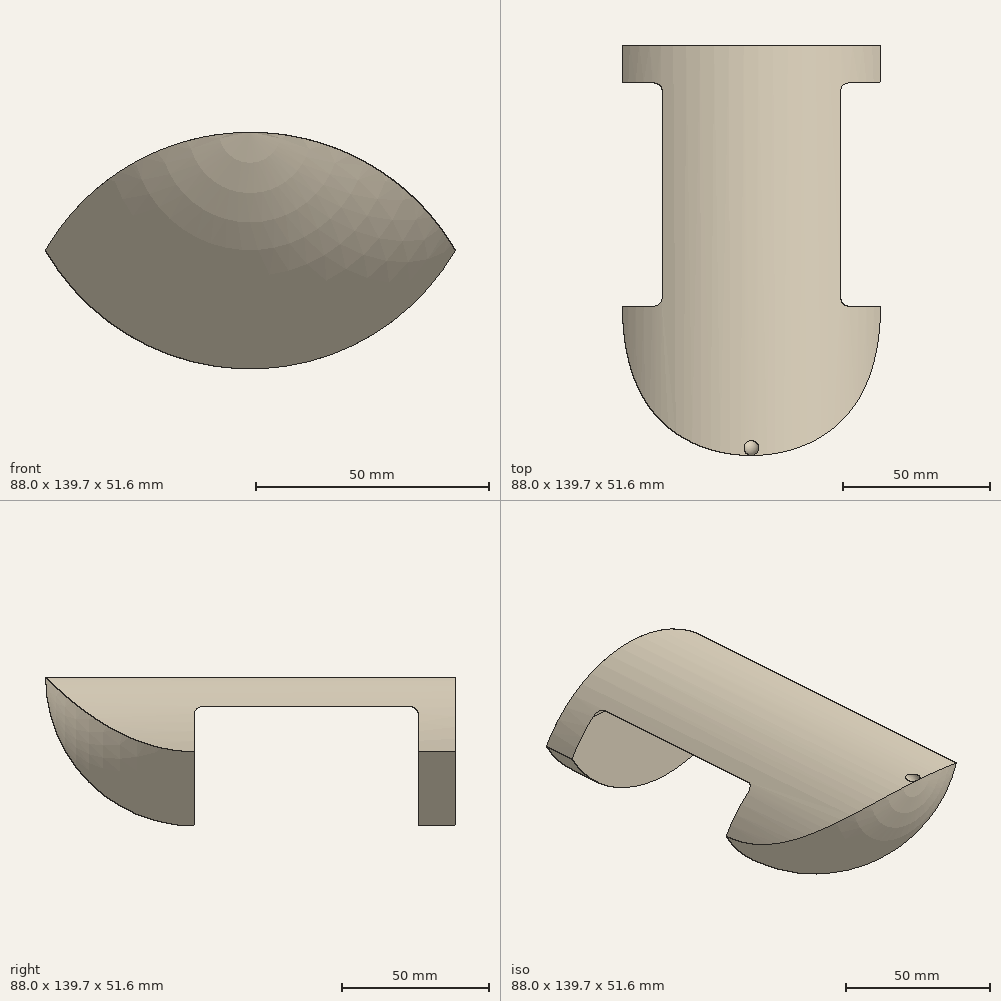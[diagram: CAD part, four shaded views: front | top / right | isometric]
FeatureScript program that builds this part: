
annotation { "Feature Type Name" : "Feature", "Feature Type Description" : "" }
export const myFeature = defineFeature(function(context is Context, id is Id, definition is map)
    precondition{}
    {
        {
            var Q0;
            Q0=qCreatedBy(makeId("Right.planeOp"),FACE);
            var sketch = newSketch(context, id + "F0", { "sketchPlane" : qUnion([Q0])});
            skLineSegment(sketch, "E0", {"start": v(0, 0) * mm, "end": v(-50.8, 0) * mm});
            skLineSegment(sketch, "E1", {"start": v(0, 0) * mm, "end": v(0, -50.8) * mm});
            skArc(sketch, "E2", {"start": v(-50.8, 0) * mm, "mid": v(-35.92, -35.92) * mm, "end": v(0, -50.8) * mm});
            skSolve(sketch);
        }
        {
            var Q0;
            Q0=makeQuery(id+"F0.imprint","IMPRINT",FACE,{"disambiguationData":[TD([[makeQuery(id+"F0.imprint","IMPRINT",EDGE,{"derivedFrom":sQuery(id+"F0.wireOp",EDGE,"E0")}),1.0]])]});
            var Q1;
            Q1=sQuery(id+"F0.wireOp",EDGE,"E0");
            revolve(context, id + "F1", {"entities" : qUnion([Q0]), "axis" : qUnion([Q1]), "revolveType" : RevolveType.SYMMETRIC, "angle" : 180 * degree});
        }
        {
            var Q0;
            Q0=qCreatedBy(makeId("Front.planeOp"),FACE);
            var sketch = newSketch(context, id + "F2", { "sketchPlane" : qUnion([Q0])});
            skPoint(sketch, "E3.0", {"position": v(50.8, 0) * mm});
            skPoint(sketch, "E4.0", {"position": v(-50.8, 0) * mm});
            skArc(sketch, "E5.0", {"start": v(50.8, 0) * mm, "mid": v(0, -50.8) * mm, "end": v(-50.8, 0) * mm});
            skLineSegment(sketch, "E6", {"start": v(50.8, 0) * mm, "end": v(50.8, -50.8) * mm, "construction": true});
            skLineSegment(sketch, "E7", {"start": v(50.8, -50.8) * mm, "end": v(-50.8, -50.8) * mm, "construction": true});
            skLineSegment(sketch, "E8", {"start": v(-50.8, -50.8) * mm, "end": v(-50.8, 0) * mm, "construction": true});
            skArc(sketch, "E9", {"start": v(50.8, -50.8) * mm, "mid": v(0, 0) * mm, "end": v(-50.8, -50.8) * mm});
            skLineSegment(sketch, "E10", {"start": v(50.8, -50.8) * mm, "end": v(50.8, 0) * mm});
            skLineSegment(sketch, "E11", {"start": v(-50.8, 0) * mm, "end": v(-50.8, -50.8) * mm});
            skSolve(sketch);
        }
        {
            var Q0;
            Q0 = qSketchRegion(id + "F2", true);
            extrude(context, id + "F3", {"entities" : qUnion([Q0]), "operationType" : NewBodyOperationType.INTERSECT, "endBound" : BoundingType.THROUGH_ALL, "depth" : 89.11 * mm});
        }
        {
            var Q0;
            Q0=makeQuery(id+"F1.opRevolve","SWEPT_FACE",FACE,{"disambiguationData":[OSD([sQuery(id+"F0.wireOp",EDGE,"E1")])]});
            extrude(context, id + "F4", {"entities" : qUnion([Q0]), "operationType" : NewBodyOperationType.ADD, "depth" : 88.9 * mm});
        }
        {
            var Q0;
            Q0=qCreatedBy(makeId("Front.planeOp"),FACE);
            var sketch = newSketch(context, id + "F5", { "sketchPlane" : qUnion([Q0])});
            skLineSegment(sketch, "E12.bottom", {"start": v(-63.5, -10.16) * mm, "end": v(63.5, -10.16) * mm});
            skLineSegment(sketch, "E12.top", {"start": v(-63.5, -73.66) * mm, "end": v(63.5, -73.66) * mm});
            skLineSegment(sketch, "E12.left", {"start": v(-63.5, -10.16) * mm, "end": v(-63.5, -73.66) * mm});
            skLineSegment(sketch, "E12.right", {"start": v(63.5, -10.16) * mm, "end": v(63.5, -73.66) * mm});
            skSolve(sketch);
        }
        {
            var Q0;
            Q0 = qSketchRegion(id + "F5", true);
            extrude(context, id + "F6", {"entities" : qUnion([Q0]), "operationType" : NewBodyOperationType.REMOVE, "oppositeDirection" : true, "depth" : 76.2 * mm});
        }
        {
            var Q0;
            Q0=qCreatedBy(makeId("Top.planeOp"),FACE);
            var sketch = newSketch(context, id + "F7", { "sketchPlane" : qUnion([Q0])});
            skFitSpline(sketch, "E13.0", {"points": [v(44, 0) * mm, v(44, -1.7) * mm, v(43.95, -3.4) * mm, v(43.85, -5.07) * mm, v(43.75, -6.75) * mm, v(43.6, -8.4) * mm, v(43.4, -10.04) * mm, v(43, -13.43) * mm, v(42.4, -16.62) * mm, v(41.58, -19.61) * mm, v(40.73, -22.74) * mm, v(39.67, -25.63) * mm, v(38.39, -28.28) * mm, v(37.05, -31.05) * mm, v(35.47, -33.57) * mm, v(33.66, -35.85) * mm, v(31.79, -38.2) * mm, v(29.67, -40.28) * mm, v(27.3, -42.1) * mm, v(26.1, -43.02) * mm, v(24.84, -43.87) * mm, v(23.52, -44.65) * mm, v(22.2, -45.44) * mm, v(20.83, -46.15) * mm, v(19.4, -46.8) * mm, v(17.95, -47.44) * mm, v(16.45, -48.02) * mm, v(14.9, -48.51) * mm, v(13.35, -49.01) * mm, v(11.77, -49.43) * mm, v(10.14, -49.77) * mm, v(8.52, -50.1) * mm, v(6.88, -50.36) * mm, v(5.22, -50.53) * mm, v(3.53, -50.7) * mm, v(1.83, -50.8) * mm, v(0.13, -50.8) * mm, v(-1.56, -50.8) * mm, v(-3.25, -50.72) * mm, v(-4.92, -50.56) * mm, v(-6.6, -50.4) * mm, v(-8.26, -50.15) * mm, v(-9.9, -49.82) * mm, v(-11.53, -49.49) * mm, v(-13.13, -49.07) * mm, v(-14.7, -48.58) * mm, v(-16.24, -48.1) * mm, v(-17.74, -47.53) * mm, v(-19.2, -46.88) * mm, v(-20.65, -46.24) * mm, v(-22.05, -45.52) * mm, v(-23.4, -44.73) * mm, v(-24.72, -43.95) * mm, v(-26, -43.1) * mm, v(-27.2, -42.17) * mm, v(-29.59, -40.35) * mm, v(-31.72, -38.26) * mm, v(-33.6, -35.92) * mm, v(-35.43, -33.64) * mm, v(-37.02, -31.11) * mm, v(-38.36, -28.34) * mm, v(-39.65, -25.68) * mm, v(-40.71, -22.8) * mm, v(-41.57, -19.66) * mm, v(-42.38, -16.67) * mm, v(-43, -13.47) * mm, v(-43.4, -10.07) * mm, v(-43.6, -8.44) * mm, v(-43.75, -6.78) * mm, v(-43.85, -5.08) * mm, v(-43.94, -3.4) * mm, v(-44, -1.7) * mm, v(-44, 0) * mm], "construction": true});
            skPoint(sketch, "E14.first.point", {"position": v(0, -50.8) * mm});
            skPoint(sketch, "E14.second.point", {"position": v(0, -50.8) * mm});
            skLineSegment(sketch, "E15", {"start": v(0, -50.8) * mm, "end": v(0, 0) * mm, "construction": true});
            skLineSegment(sketch, "E16", {"start": v(0, 0) * mm, "end": v(0.1, 0.91) * mm, "construction": true});
            skArc(sketch, "E17", {"start": v(0, -45.72) * mm, "mid": v(-2.54, -48.26) * mm, "end": v(0, -50.8) * mm});
            skLineSegment(sketch, "E18", {"start": v(0, -50.8) * mm, "end": v(0, -45.72) * mm});
            skSolve(sketch);
        }
        {
            var Q0;
            Q0 = qSketchRegion(id + "F7", true);
            var Q1;
            Q1=makeQuery(id+"F7.imprint","IMPRINT",FACE,{"disambiguationData":[TD([[makeQuery(id+"F7.imprint","IMPRINT",EDGE,{"derivedFrom":sQuery(id+"F7.wireOp",EDGE,"E17")}),1.0]])]});
            var Q2;
            Q2=sQuery(id+"F7.wireOp",EDGE,"E15");
            revolve(context, id + "F8", {"operationType" : NewBodyOperationType.ADD, "entities" : qUnion([Q0, Q1]), "axis" : qUnion([Q2]), "revolveType" : RevolveType.FULL});
        }
        {
            var Q0;
            Q0=makeQuery(id+"F6.boolean.opBoolean","COPY",EDGE,{"derivedFrom":makeQuery(id+"F6.opExtrude","CAP_EDGE",EDGE,{"disambiguationData":[OSD([sQuery(id+"F5.wireOp",EDGE,"E12.bottom")])],"isStart":true})});
            var Q1;
            Q1=makeQuery(id+"F6.boolean.opBoolean","COPY",EDGE,{"derivedFrom":makeQuery(id+"F6.opExtrude","CAP_EDGE",EDGE,{"disambiguationData":[OSD([sQuery(id+"F5.wireOp",EDGE,"E12.bottom")])],"isStart":false})});
            fillet(context, id + "F9", {"entities" : qUnion([Q0, Q1]), "radius" : 2.54 * mm, "tangentPropagation" : true, "allowEdgeOverflow" : false});
        }
    });
